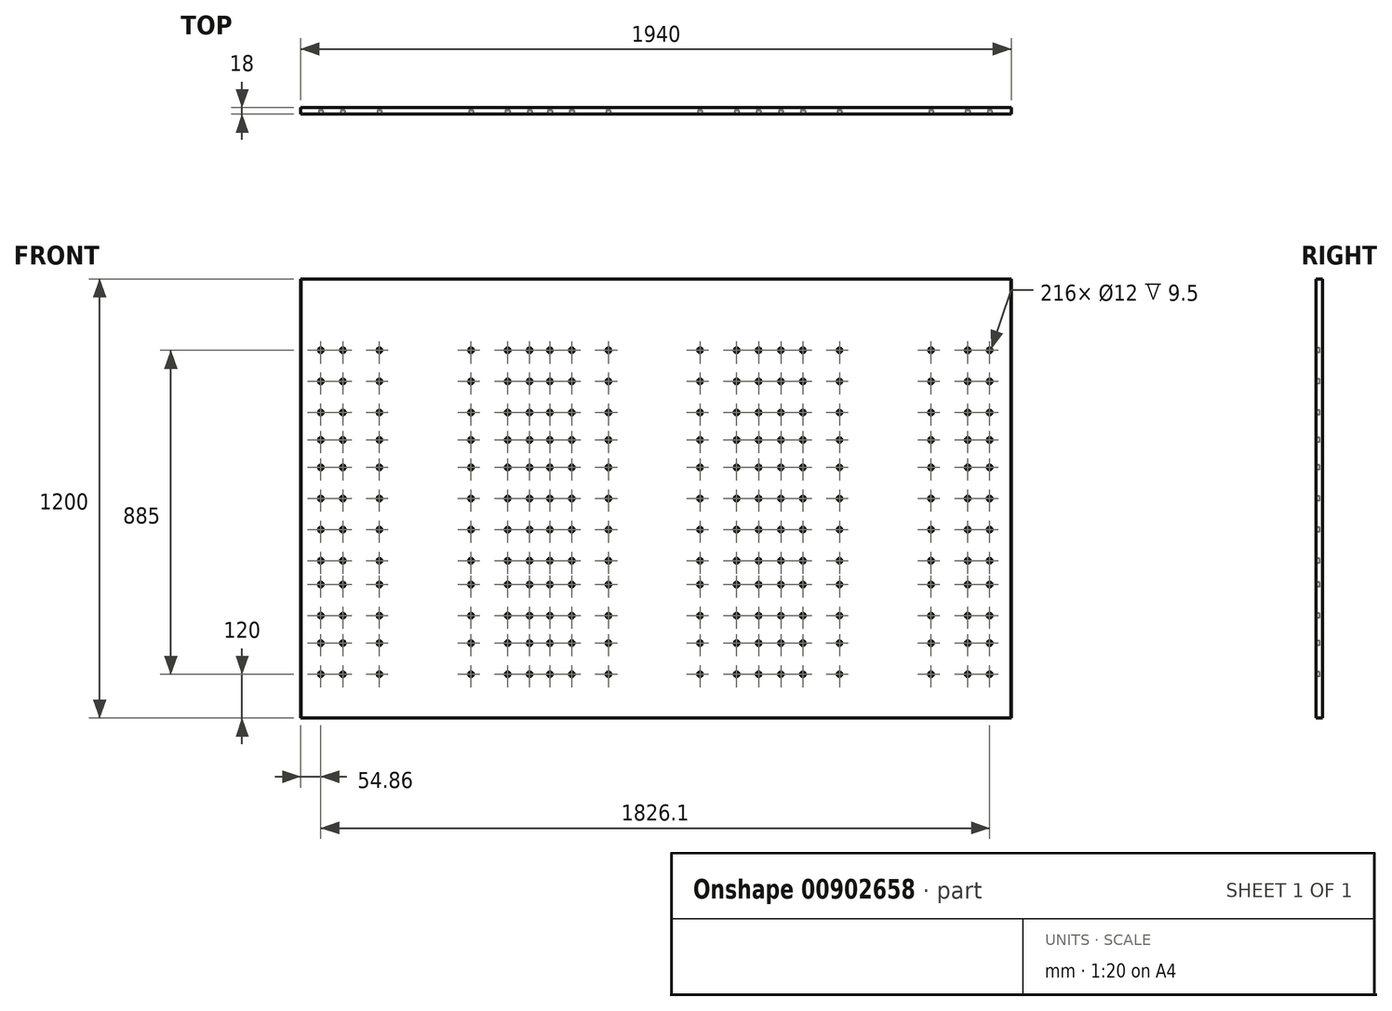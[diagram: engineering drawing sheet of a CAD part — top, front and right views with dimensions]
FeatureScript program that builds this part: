
annotation { "Feature Type Name" : "Feature", "Feature Type Description" : "" }
export const myFeature = defineFeature(function(context is Context, id is Id, definition is map)
    precondition{}
    {
        {
            var Q0;
            Q0=qCreatedBy(makeId("Front.planeOp"),FACE);
            var sketch = newSketch(context, id + "F0", { "sketchPlane" : qUnion([Q0])});
            skLineSegment(sketch, "E0.bottom", {"start": v(0, 0) * mm, "end": v(1940, 0) * mm});
            skLineSegment(sketch, "E0.top", {"start": v(0, 1200) * mm, "end": v(1940, 1200) * mm});
            skLineSegment(sketch, "E0.left", {"start": v(0, 0) * mm, "end": v(0, 1200) * mm});
            skLineSegment(sketch, "E0.right", {"start": v(1940, 0) * mm, "end": v(1940, 1200) * mm});
            skSolve(sketch);
        }
        {
            var Q0;
            Q0 = qSketchRegion(id + "F0", true);
            extrude(context, id + "F1", {"entities" : qUnion([Q0]), "depth" : 18 * mm, "offsetDistance" : 25 * mm});
        }
        {
            var Q0;
            Q0=makeQuery(id+"F1.opExtrude","CAP_FACE",FACE,{"disambiguationData":[OSD([sQuery(id+"F0.wireOp",EDGE,"E0.bottom"),sQuery(id+"F0.wireOp",EDGE,"E0.top"),sQuery(id+"F0.wireOp",EDGE,"E0.left"),sQuery(id+"F0.wireOp",EDGE,"E0.right")])],"isStart":false});
            var sketch = newSketch(context, id + "F2", { "sketchPlane" : qUnion([Q0])});
            skLineSegment(sketch, "E1", {"start": v(0, 920) * mm, "end": v(1940, 920) * mm, "construction": true});
            skLineSegment(sketch, "E2", {"start": v(0, 840) * mm, "end": v(1940, 840) * mm, "construction": true});
            skLineSegment(sketch, "E3", {"start": v(0, 760) * mm, "end": v(1940, 760) * mm, "construction": true});
            skLineSegment(sketch, "E4", {"start": v(0, 680) * mm, "end": v(1940, 680) * mm, "construction": true});
            skLineSegment(sketch, "E5", {"start": v(0, 1005) * mm, "end": v(1940, 1005) * mm, "construction": true});
            skLineSegment(sketch, "E6", {"start": v(0, 600) * mm, "end": v(1940, 600) * mm, "construction": true});
            skLineSegment(sketch, "E7", {"start": v(0, 520) * mm, "end": v(1940, 520) * mm, "construction": true});
            skLineSegment(sketch, "E8", {"start": v(1940, 520) * mm, "end": v(1940, 440) * mm, "construction": true});
            skLineSegment(sketch, "E9", {"start": v(1940, 440) * mm, "end": v(0, 440) * mm, "construction": true});
            skLineSegment(sketch, "E10", {"start": v(0, 440) * mm, "end": v(0, 360) * mm, "construction": true});
            skLineSegment(sketch, "E11", {"start": v(0, 360) * mm, "end": v(1940, 360) * mm, "construction": true});
            skLineSegment(sketch, "E12", {"start": v(1940, 360) * mm, "end": v(1940, 280) * mm, "construction": true});
            skLineSegment(sketch, "E13", {"start": v(1940, 280) * mm, "end": v(0, 280) * mm, "construction": true});
            skLineSegment(sketch, "E14", {"start": v(0, 280) * mm, "end": v(0, 200) * mm, "construction": true});
            skLineSegment(sketch, "E15", {"start": v(0, 200) * mm, "end": v(1940, 200) * mm, "construction": true});
            skLineSegment(sketch, "E16", {"start": v(1940, 200) * mm, "end": v(1940, 120) * mm, "construction": true});
            skLineSegment(sketch, "E17", {"start": v(1940, 120) * mm, "end": v(0, 120) * mm, "construction": true});
            skCircle(sketch, "E18", {"center": v(54.86, 1005) * mm, "radius": 6 * mm});
            skCircle(sketch, "E19", {"center": v(114.86, 1005) * mm, "radius": 6 * mm});
            skCircle(sketch, "E20", {"center": v(214.86, 1005) * mm, "radius": 6 * mm});
            skCircle(sketch, "E21", {"center": v(464.86, 1005) * mm, "radius": 6 * mm});
            skCircle(sketch, "E22", {"center": v(564.86, 1005) * mm, "radius": 6 * mm});
            skCircle(sketch, "E23", {"center": v(624.86, 1005) * mm, "radius": 6 * mm});
            skCircle(sketch, "E24.MirrorC", {"center": v(114.86, 835) * mm, "radius": 6 * mm});
            skCircle(sketch, "E25.MirrorC", {"center": v(214.86, 835) * mm, "radius": 6 * mm});
            skCircle(sketch, "E26.MirrorC", {"center": v(54.86, 835) * mm, "radius": 6 * mm});
            skCircle(sketch, "E27.MirrorC", {"center": v(624.86, 835) * mm, "radius": 6 * mm});
            skCircle(sketch, "E28.MirrorC", {"center": v(564.86, 835) * mm, "radius": 6 * mm});
            skCircle(sketch, "E29.MirrorC", {"center": v(464.86, 835) * mm, "radius": 6 * mm});
            skCircle(sketch, "E30", {"center": v(54.86, 920) * mm, "radius": 6 * mm});
            skCircle(sketch, "E31", {"center": v(114.86, 920) * mm, "radius": 6 * mm});
            skCircle(sketch, "E32", {"center": v(214.86, 920) * mm, "radius": 6 * mm});
            skCircle(sketch, "E33", {"center": v(464.86, 920) * mm, "radius": 6 * mm});
            skCircle(sketch, "E34", {"center": v(564.86, 920) * mm, "radius": 6 * mm});
            skCircle(sketch, "E35", {"center": v(624.86, 920) * mm, "radius": 6 * mm});
            skCircle(sketch, "E36.MirrorC", {"center": v(624.86, 600) * mm, "radius": 6 * mm});
            skCircle(sketch, "E37.MirrorC", {"center": v(54.86, 600) * mm, "radius": 6 * mm});
            skCircle(sketch, "E38.MirrorC", {"center": v(564.86, 600) * mm, "radius": 6 * mm});
            skCircle(sketch, "E39.MirrorC", {"center": v(214.86, 600) * mm, "radius": 6 * mm});
            skCircle(sketch, "E40.MirrorC", {"center": v(114.86, 600) * mm, "radius": 6 * mm});
            skCircle(sketch, "E41.MirrorC", {"center": v(464.86, 600) * mm, "radius": 6 * mm});
            skCircle(sketch, "E42.MirrorC", {"center": v(464.86, 685) * mm, "radius": 6 * mm});
            skCircle(sketch, "E43.MirrorC", {"center": v(564.86, 685) * mm, "radius": 6 * mm});
            skCircle(sketch, "E44.MirrorC", {"center": v(54.86, 685) * mm, "radius": 6 * mm});
            skCircle(sketch, "E45.MirrorC", {"center": v(624.86, 685) * mm, "radius": 6 * mm});
            skCircle(sketch, "E46.MirrorC", {"center": v(214.86, 685) * mm, "radius": 6 * mm});
            skCircle(sketch, "E47.MirrorC", {"center": v(114.86, 685) * mm, "radius": 6 * mm});
            skCircle(sketch, "E48.MirrorC", {"center": v(624.86, 515) * mm, "radius": 6 * mm});
            skCircle(sketch, "E49.MirrorC", {"center": v(214.86, 515) * mm, "radius": 6 * mm});
            skCircle(sketch, "E50.MirrorC", {"center": v(114.86, 515) * mm, "radius": 6 * mm});
            skCircle(sketch, "E51.MirrorC", {"center": v(564.86, 515) * mm, "radius": 6 * mm});
            skCircle(sketch, "E52.MirrorC", {"center": v(54.86, 515) * mm, "radius": 6 * mm});
            skCircle(sketch, "E53.MirrorC", {"center": v(464.86, 515) * mm, "radius": 6 * mm});
            skLineSegment(sketch, "E54.MirrorCS", {"start": v(0, 515) * mm, "end": v(1940, 515) * mm, "construction": true});
            skCircle(sketch, "E55.MirrorC", {"center": v(54.86, 760) * mm, "radius": 6 * mm});
            skCircle(sketch, "E56.MirrorC", {"center": v(564.86, 760) * mm, "radius": 6 * mm});
            skCircle(sketch, "E57.MirrorC", {"center": v(624.86, 760) * mm, "radius": 6 * mm});
            skCircle(sketch, "E58.MirrorC", {"center": v(464.86, 760) * mm, "radius": 6 * mm});
            skCircle(sketch, "E59.MirrorC", {"center": v(114.86, 760) * mm, "radius": 6 * mm});
            skCircle(sketch, "E60.MirrorC", {"center": v(214.86, 760) * mm, "radius": 6 * mm});
            skCircle(sketch, "E61.MirrorC", {"center": v(54.86, 205) * mm, "radius": 6 * mm});
            skCircle(sketch, "E62.MirrorC", {"center": v(624.86, 205) * mm, "radius": 6 * mm});
            skCircle(sketch, "E63.MirrorC", {"center": v(214.86, 205) * mm, "radius": 6 * mm});
            skCircle(sketch, "E64.MirrorC", {"center": v(114.86, 205) * mm, "radius": 6 * mm});
            skCircle(sketch, "E65.MirrorC", {"center": v(564.86, 205) * mm, "radius": 6 * mm});
            skCircle(sketch, "E66.MirrorC", {"center": v(464.86, 205) * mm, "radius": 6 * mm});
            skLineSegment(sketch, "E67.MirrorCS", {"start": v(0, 205) * mm, "end": v(1940, 205) * mm, "construction": true});
            skCircle(sketch, "E68.MirrorC", {"center": v(114.86, 365) * mm, "radius": 6 * mm});
            skCircle(sketch, "E69.MirrorC", {"center": v(624.86, 365) * mm, "radius": 6 * mm});
            skCircle(sketch, "E70.MirrorC", {"center": v(564.86, 365) * mm, "radius": 6 * mm});
            skCircle(sketch, "E71.MirrorC", {"center": v(54.86, 365) * mm, "radius": 6 * mm});
            skCircle(sketch, "E72.MirrorC", {"center": v(464.86, 365) * mm, "radius": 6 * mm});
            skCircle(sketch, "E73.MirrorC", {"center": v(214.86, 365) * mm, "radius": 6 * mm});
            skLineSegment(sketch, "E74.MirrorCS", {"start": v(0, 365) * mm, "end": v(1940, 365) * mm, "construction": true});
            skLineSegment(sketch, "E75.MirrorCS", {"start": v(0, 280) * mm, "end": v(1940, 280) * mm, "construction": true});
            skCircle(sketch, "E76.MirrorC", {"center": v(564.86, 280) * mm, "radius": 6 * mm});
            skCircle(sketch, "E77.MirrorC", {"center": v(54.86, 280) * mm, "radius": 6 * mm});
            skCircle(sketch, "E78.MirrorC", {"center": v(214.86, 280) * mm, "radius": 6 * mm});
            skCircle(sketch, "E79.MirrorC", {"center": v(624.86, 280) * mm, "radius": 6 * mm});
            skCircle(sketch, "E80.MirrorC", {"center": v(114.86, 280) * mm, "radius": 6 * mm});
            skCircle(sketch, "E81.MirrorC", {"center": v(464.86, 280) * mm, "radius": 6 * mm});
            skLineSegment(sketch, "E82.MirrorCS", {"start": v(0, 120) * mm, "end": v(1940, 120) * mm, "construction": true});
            skCircle(sketch, "E83.MirrorC", {"center": v(54.86, 120) * mm, "radius": 6 * mm});
            skCircle(sketch, "E84.MirrorC", {"center": v(114.86, 120) * mm, "radius": 6 * mm});
            skCircle(sketch, "E85.MirrorC", {"center": v(214.86, 120) * mm, "radius": 6 * mm});
            skCircle(sketch, "E86.MirrorC", {"center": v(624.86, 120) * mm, "radius": 6 * mm});
            skCircle(sketch, "E87.MirrorC", {"center": v(564.86, 120) * mm, "radius": 6 * mm});
            skCircle(sketch, "E88.MirrorC", {"center": v(464.86, 120) * mm, "radius": 6 * mm});
            skLineSegment(sketch, "E89.MirrorCS", {"start": v(0, 430) * mm, "end": v(1940, 430) * mm, "construction": true});
            skCircle(sketch, "E90.MirrorC", {"center": v(624.86, 430) * mm, "radius": 6 * mm});
            skCircle(sketch, "E91.MirrorC", {"center": v(214.86, 430) * mm, "radius": 6 * mm});
            skCircle(sketch, "E92.MirrorC", {"center": v(564.86, 430) * mm, "radius": 6 * mm});
            skCircle(sketch, "E93.MirrorC", {"center": v(114.86, 430) * mm, "radius": 6 * mm});
            skCircle(sketch, "E94.MirrorC", {"center": v(464.86, 430) * mm, "radius": 6 * mm});
            skCircle(sketch, "E95.MirrorC", {"center": v(54.86, 430) * mm, "radius": 6 * mm});
            skLineSegment(sketch, "E96", {"start": v(652.48, 0) * mm, "end": v(652.48, 1200) * mm, "construction": true});
            skCircle(sketch, "E97.MirrorC", {"center": v(1250.1, 1005) * mm, "radius": 6 * mm});
            skCircle(sketch, "E98.MirrorC", {"center": v(740.1, 685) * mm, "radius": 6 * mm});
            skCircle(sketch, "E99.MirrorC", {"center": v(740.1, 365) * mm, "radius": 6 * mm});
            skCircle(sketch, "E100.MirrorC", {"center": v(680.1, 515) * mm, "radius": 6 * mm});
            skCircle(sketch, "E101.MirrorC", {"center": v(680.1, 685) * mm, "radius": 6 * mm});
            skCircle(sketch, "E102.MirrorC", {"center": v(1090.1, 205) * mm, "radius": 6 * mm});
            skCircle(sketch, "E103.MirrorC", {"center": v(1190.1, 685) * mm, "radius": 6 * mm});
            skCircle(sketch, "E104.MirrorC", {"center": v(740.1, 205) * mm, "radius": 6 * mm});
            skCircle(sketch, "E105.MirrorC", {"center": v(1250.1, 205) * mm, "radius": 6 * mm});
            skCircle(sketch, "E106.MirrorC", {"center": v(1250.1, 515) * mm, "radius": 6 * mm});
            skCircle(sketch, "E107.MirrorC", {"center": v(1190.1, 205) * mm, "radius": 6 * mm});
            skCircle(sketch, "E108.MirrorC", {"center": v(840.1, 1005) * mm, "radius": 6 * mm});
            skCircle(sketch, "E109.MirrorC", {"center": v(840.1, 365) * mm, "radius": 6 * mm});
            skCircle(sketch, "E110.MirrorC", {"center": v(1190.1, 365) * mm, "radius": 6 * mm});
            skCircle(sketch, "E111.MirrorC", {"center": v(680.1, 1005) * mm, "radius": 6 * mm});
            skCircle(sketch, "E112.MirrorC", {"center": v(840.1, 685) * mm, "radius": 6 * mm});
            skCircle(sketch, "E113.MirrorC", {"center": v(1090.1, 1005) * mm, "radius": 6 * mm});
            skCircle(sketch, "E114.MirrorC", {"center": v(740.1, 1005) * mm, "radius": 6 * mm});
            skCircle(sketch, "E115.MirrorC", {"center": v(1190.1, 835) * mm, "radius": 6 * mm});
            skCircle(sketch, "E116.MirrorC", {"center": v(740.1, 835) * mm, "radius": 6 * mm});
            skCircle(sketch, "E117.MirrorC", {"center": v(1090.1, 365) * mm, "radius": 6 * mm});
            skCircle(sketch, "E118.MirrorC", {"center": v(1190.1, 515) * mm, "radius": 6 * mm});
            skCircle(sketch, "E119.MirrorC", {"center": v(1090.1, 515) * mm, "radius": 6 * mm});
            skCircle(sketch, "E120.MirrorC", {"center": v(680.1, 205) * mm, "radius": 6 * mm});
            skCircle(sketch, "E121.MirrorC", {"center": v(680.1, 365) * mm, "radius": 6 * mm});
            skCircle(sketch, "E122.MirrorC", {"center": v(840.1, 515) * mm, "radius": 6 * mm});
            skCircle(sketch, "E123.MirrorC", {"center": v(1250.1, 835) * mm, "radius": 6 * mm});
            skCircle(sketch, "E124.MirrorC", {"center": v(740.1, 515) * mm, "radius": 6 * mm});
            skCircle(sketch, "E125.MirrorC", {"center": v(1090.1, 685) * mm, "radius": 6 * mm});
            skCircle(sketch, "E126.MirrorC", {"center": v(680.1, 835) * mm, "radius": 6 * mm});
            skCircle(sketch, "E127.MirrorC", {"center": v(840.1, 835) * mm, "radius": 6 * mm});
            skCircle(sketch, "E128.MirrorC", {"center": v(1090.1, 835) * mm, "radius": 6 * mm});
            skCircle(sketch, "E129.MirrorC", {"center": v(840.1, 205) * mm, "radius": 6 * mm});
            skCircle(sketch, "E130.MirrorC", {"center": v(1190.1, 1005) * mm, "radius": 6 * mm});
            skCircle(sketch, "E131.MirrorC", {"center": v(1250.1, 365) * mm, "radius": 6 * mm});
            skCircle(sketch, "E132.MirrorC", {"center": v(1250.1, 685) * mm, "radius": 6 * mm});
            skCircle(sketch, "E133.MirrorC", {"center": v(840.1, 430) * mm, "radius": 6 * mm});
            skCircle(sketch, "E134.MirrorC", {"center": v(680.1, 430) * mm, "radius": 6 * mm});
            skCircle(sketch, "E135.MirrorC", {"center": v(1250.1, 280) * mm, "radius": 6 * mm});
            skCircle(sketch, "E136.MirrorC", {"center": v(1190.1, 760) * mm, "radius": 6 * mm});
            skCircle(sketch, "E137.MirrorC", {"center": v(1090.1, 280) * mm, "radius": 6 * mm});
            skCircle(sketch, "E138.MirrorC", {"center": v(840.1, 920) * mm, "radius": 6 * mm});
            skCircle(sketch, "E139.MirrorC", {"center": v(840.1, 120) * mm, "radius": 6 * mm});
            skCircle(sketch, "E140.MirrorC", {"center": v(840.1, 600) * mm, "radius": 6 * mm});
            skCircle(sketch, "E141.MirrorC", {"center": v(740.1, 280) * mm, "radius": 6 * mm});
            skCircle(sketch, "E142.MirrorC", {"center": v(1190.1, 280) * mm, "radius": 6 * mm});
            skCircle(sketch, "E143.MirrorC", {"center": v(1250.1, 430) * mm, "radius": 6 * mm});
            skCircle(sketch, "E144.MirrorC", {"center": v(840.1, 760) * mm, "radius": 6 * mm});
            skCircle(sketch, "E145.MirrorC", {"center": v(1090.1, 120) * mm, "radius": 6 * mm});
            skCircle(sketch, "E146.MirrorC", {"center": v(1090.1, 430) * mm, "radius": 6 * mm});
            skCircle(sketch, "E147.MirrorC", {"center": v(740.1, 920) * mm, "radius": 6 * mm});
            skCircle(sketch, "E148.MirrorC", {"center": v(680.1, 760) * mm, "radius": 6 * mm});
            skCircle(sketch, "E149.MirrorC", {"center": v(1190.1, 920) * mm, "radius": 6 * mm});
            skCircle(sketch, "E150.MirrorC", {"center": v(740.1, 600) * mm, "radius": 6 * mm});
            skCircle(sketch, "E151.MirrorC", {"center": v(1090.1, 760) * mm, "radius": 6 * mm});
            skCircle(sketch, "E152.MirrorC", {"center": v(680.1, 120) * mm, "radius": 6 * mm});
            skCircle(sketch, "E153.MirrorC", {"center": v(1190.1, 120) * mm, "radius": 6 * mm});
            skCircle(sketch, "E154.MirrorC", {"center": v(680.1, 280) * mm, "radius": 6 * mm});
            skCircle(sketch, "E155.MirrorC", {"center": v(1250.1, 600) * mm, "radius": 6 * mm});
            skCircle(sketch, "E156.MirrorC", {"center": v(1250.1, 120) * mm, "radius": 6 * mm});
            skCircle(sketch, "E157.MirrorC", {"center": v(1250.1, 760) * mm, "radius": 6 * mm});
            skCircle(sketch, "E158.MirrorC", {"center": v(1250.1, 920) * mm, "radius": 6 * mm});
            skCircle(sketch, "E159.MirrorC", {"center": v(840.1, 280) * mm, "radius": 6 * mm});
            skCircle(sketch, "E160.MirrorC", {"center": v(740.1, 430) * mm, "radius": 6 * mm});
            skCircle(sketch, "E161.MirrorC", {"center": v(740.1, 120) * mm, "radius": 6 * mm});
            skCircle(sketch, "E162.MirrorC", {"center": v(1090.1, 600) * mm, "radius": 6 * mm});
            skCircle(sketch, "E163.MirrorC", {"center": v(680.1, 920) * mm, "radius": 6 * mm});
            skCircle(sketch, "E164.MirrorC", {"center": v(680.1, 600) * mm, "radius": 6 * mm});
            skCircle(sketch, "E165.MirrorC", {"center": v(740.1, 760) * mm, "radius": 6 * mm});
            skCircle(sketch, "E166.MirrorC", {"center": v(1090.1, 920) * mm, "radius": 6 * mm});
            skCircle(sketch, "E167.MirrorC", {"center": v(1190.1, 600) * mm, "radius": 6 * mm});
            skCircle(sketch, "E168.MirrorC", {"center": v(1190.1, 430) * mm, "radius": 6 * mm});
            skLineSegment(sketch, "E169", {"start": v(1280.53, 0) * mm, "end": v(1280.53, 1200) * mm, "construction": true});
            skCircle(sketch, "E170.MirrorC", {"center": v(1820.96, 835) * mm, "radius": 6 * mm});
            skCircle(sketch, "E171.MirrorC", {"center": v(1880.96, 205) * mm, "radius": 6 * mm});
            skCircle(sketch, "E172.MirrorC", {"center": v(1470.96, 1005) * mm, "radius": 6 * mm});
            skCircle(sketch, "E173.MirrorC", {"center": v(1720.96, 685) * mm, "radius": 6 * mm});
            skCircle(sketch, "E174.MirrorC", {"center": v(1310.96, 1005) * mm, "radius": 6 * mm});
            skCircle(sketch, "E175.MirrorC", {"center": v(1310.96, 515) * mm, "radius": 6 * mm});
            skCircle(sketch, "E176.MirrorC", {"center": v(1470.96, 515) * mm, "radius": 6 * mm});
            skCircle(sketch, "E177.MirrorC", {"center": v(1820.96, 1005) * mm, "radius": 6 * mm});
            skCircle(sketch, "E178.MirrorC", {"center": v(1470.96, 365) * mm, "radius": 6 * mm});
            skCircle(sketch, "E179.MirrorC", {"center": v(1720.96, 365) * mm, "radius": 6 * mm});
            skCircle(sketch, "E180.MirrorC", {"center": v(1370.96, 835) * mm, "radius": 6 * mm});
            skCircle(sketch, "E181.MirrorC", {"center": v(1370.96, 685) * mm, "radius": 6 * mm});
            skCircle(sketch, "E182.MirrorC", {"center": v(1470.96, 685) * mm, "radius": 6 * mm});
            skCircle(sketch, "E183.MirrorC", {"center": v(1880.96, 835) * mm, "radius": 6 * mm});
            skCircle(sketch, "E184.MirrorC", {"center": v(1720.96, 205) * mm, "radius": 6 * mm});
            skCircle(sketch, "E185.MirrorC", {"center": v(1820.96, 365) * mm, "radius": 6 * mm});
            skCircle(sketch, "E186.MirrorC", {"center": v(1720.96, 835) * mm, "radius": 6 * mm});
            skCircle(sketch, "E187.MirrorC", {"center": v(1470.96, 205) * mm, "radius": 6 * mm});
            skCircle(sketch, "E188.MirrorC", {"center": v(1310.96, 205) * mm, "radius": 6 * mm});
            skCircle(sketch, "E189.MirrorC", {"center": v(1370.96, 205) * mm, "radius": 6 * mm});
            skCircle(sketch, "E190.MirrorC", {"center": v(1880.96, 685) * mm, "radius": 6 * mm});
            skCircle(sketch, "E191.MirrorC", {"center": v(1370.96, 1005) * mm, "radius": 6 * mm});
            skCircle(sketch, "E192.MirrorC", {"center": v(1370.96, 515) * mm, "radius": 6 * mm});
            skCircle(sketch, "E193.MirrorC", {"center": v(1310.96, 365) * mm, "radius": 6 * mm});
            skCircle(sketch, "E194.MirrorC", {"center": v(1880.96, 515) * mm, "radius": 6 * mm});
            skCircle(sketch, "E195.MirrorC", {"center": v(1880.96, 365) * mm, "radius": 6 * mm});
            skCircle(sketch, "E196.MirrorC", {"center": v(1820.96, 685) * mm, "radius": 6 * mm});
            skCircle(sketch, "E197.MirrorC", {"center": v(1880.96, 1005) * mm, "radius": 6 * mm});
            skCircle(sketch, "E198.MirrorC", {"center": v(1370.96, 365) * mm, "radius": 6 * mm});
            skCircle(sketch, "E199.MirrorC", {"center": v(1820.96, 205) * mm, "radius": 6 * mm});
            skCircle(sketch, "E200.MirrorC", {"center": v(1720.96, 1005) * mm, "radius": 6 * mm});
            skCircle(sketch, "E201.MirrorC", {"center": v(1820.96, 515) * mm, "radius": 6 * mm});
            skCircle(sketch, "E202.MirrorC", {"center": v(1470.96, 835) * mm, "radius": 6 * mm});
            skCircle(sketch, "E203.MirrorC", {"center": v(1310.96, 685) * mm, "radius": 6 * mm});
            skCircle(sketch, "E204.MirrorC", {"center": v(1310.96, 835) * mm, "radius": 6 * mm});
            skCircle(sketch, "E205.MirrorC", {"center": v(1720.96, 515) * mm, "radius": 6 * mm});
            skCircle(sketch, "E206.MirrorC", {"center": v(1880.96, 600) * mm, "radius": 6 * mm});
            skCircle(sketch, "E207.MirrorC", {"center": v(1720.96, 600) * mm, "radius": 6 * mm});
            skCircle(sketch, "E208.MirrorC", {"center": v(1820.96, 120) * mm, "radius": 6 * mm});
            skCircle(sketch, "E209.MirrorC", {"center": v(1470.96, 760) * mm, "radius": 6 * mm});
            skCircle(sketch, "E210.MirrorC", {"center": v(1820.96, 280) * mm, "radius": 6 * mm});
            skCircle(sketch, "E211.MirrorC", {"center": v(1370.96, 430) * mm, "radius": 6 * mm});
            skCircle(sketch, "E212.MirrorC", {"center": v(1880.96, 120) * mm, "radius": 6 * mm});
            skCircle(sketch, "E213.MirrorC", {"center": v(1370.96, 920) * mm, "radius": 6 * mm});
            skCircle(sketch, "E214.MirrorC", {"center": v(1370.96, 120) * mm, "radius": 6 * mm});
            skCircle(sketch, "E215.MirrorC", {"center": v(1820.96, 920) * mm, "radius": 6 * mm});
            skCircle(sketch, "E216.MirrorC", {"center": v(1820.96, 600) * mm, "radius": 6 * mm});
            skCircle(sketch, "E217.MirrorC", {"center": v(1310.96, 280) * mm, "radius": 6 * mm});
            skCircle(sketch, "E218.MirrorC", {"center": v(1310.96, 760) * mm, "radius": 6 * mm});
            skCircle(sketch, "E219.MirrorC", {"center": v(1880.96, 920) * mm, "radius": 6 * mm});
            skCircle(sketch, "E220.MirrorC", {"center": v(1370.96, 600) * mm, "radius": 6 * mm});
            skCircle(sketch, "E221.MirrorC", {"center": v(1310.96, 120) * mm, "radius": 6 * mm});
            skCircle(sketch, "E222.MirrorC", {"center": v(1310.96, 430) * mm, "radius": 6 * mm});
            skCircle(sketch, "E223.MirrorC", {"center": v(1720.96, 920) * mm, "radius": 6 * mm});
            skCircle(sketch, "E224.MirrorC", {"center": v(1310.96, 600) * mm, "radius": 6 * mm});
            skCircle(sketch, "E225.MirrorC", {"center": v(1370.96, 760) * mm, "radius": 6 * mm});
            skCircle(sketch, "E226.MirrorC", {"center": v(1720.96, 760) * mm, "radius": 6 * mm});
            skCircle(sketch, "E227.MirrorC", {"center": v(1720.96, 430) * mm, "radius": 6 * mm});
            skCircle(sketch, "E228.MirrorC", {"center": v(1820.96, 760) * mm, "radius": 6 * mm});
            skCircle(sketch, "E229.MirrorC", {"center": v(1470.96, 920) * mm, "radius": 6 * mm});
            skCircle(sketch, "E230.MirrorC", {"center": v(1470.96, 120) * mm, "radius": 6 * mm});
            skCircle(sketch, "E231.MirrorC", {"center": v(1310.96, 920) * mm, "radius": 6 * mm});
            skCircle(sketch, "E232.MirrorC", {"center": v(1880.96, 430) * mm, "radius": 6 * mm});
            skCircle(sketch, "E233.MirrorC", {"center": v(1720.96, 280) * mm, "radius": 6 * mm});
            skCircle(sketch, "E234.MirrorC", {"center": v(1880.96, 280) * mm, "radius": 6 * mm});
            skCircle(sketch, "E235.MirrorC", {"center": v(1370.96, 280) * mm, "radius": 6 * mm});
            skCircle(sketch, "E236.MirrorC", {"center": v(1880.96, 760) * mm, "radius": 6 * mm});
            skCircle(sketch, "E237.MirrorC", {"center": v(1470.96, 600) * mm, "radius": 6 * mm});
            skCircle(sketch, "E238.MirrorC", {"center": v(1470.96, 430) * mm, "radius": 6 * mm});
            skCircle(sketch, "E239.MirrorC", {"center": v(1470.96, 280) * mm, "radius": 6 * mm});
            skCircle(sketch, "E240.MirrorC", {"center": v(1720.96, 120) * mm, "radius": 6 * mm});
            skCircle(sketch, "E241.MirrorC", {"center": v(1820.96, 430) * mm, "radius": 6 * mm});
            skSolve(sketch);
        }
        {
            var Q0;
            Q0 = qSketchRegion(id + "F2", true);
            extrude(context, id + "F3", {"entities" : qUnion([Q0]), "operationType" : NewBodyOperationType.REMOVE, "oppositeDirection" : true, "depth" : 10 * mm, "offsetDistance" : 25 * mm});
        }
        {
            var Q0;
            Q0=makeQuery(id+"F1.opExtrude","CAP_FACE",FACE,{"disambiguationData":[OSD([sQuery(id+"F0.wireOp",EDGE,"E0.bottom"),sQuery(id+"F0.wireOp",EDGE,"E0.top"),sQuery(id+"F0.wireOp",EDGE,"E0.left"),sQuery(id+"F0.wireOp",EDGE,"E0.right")])],"isStart":false});
            chamfer(context, id + "F4", {"entities" : qUnion([Q0]), "width" : .5 * mm, "tangentPropagation" : true});
        }
    });
